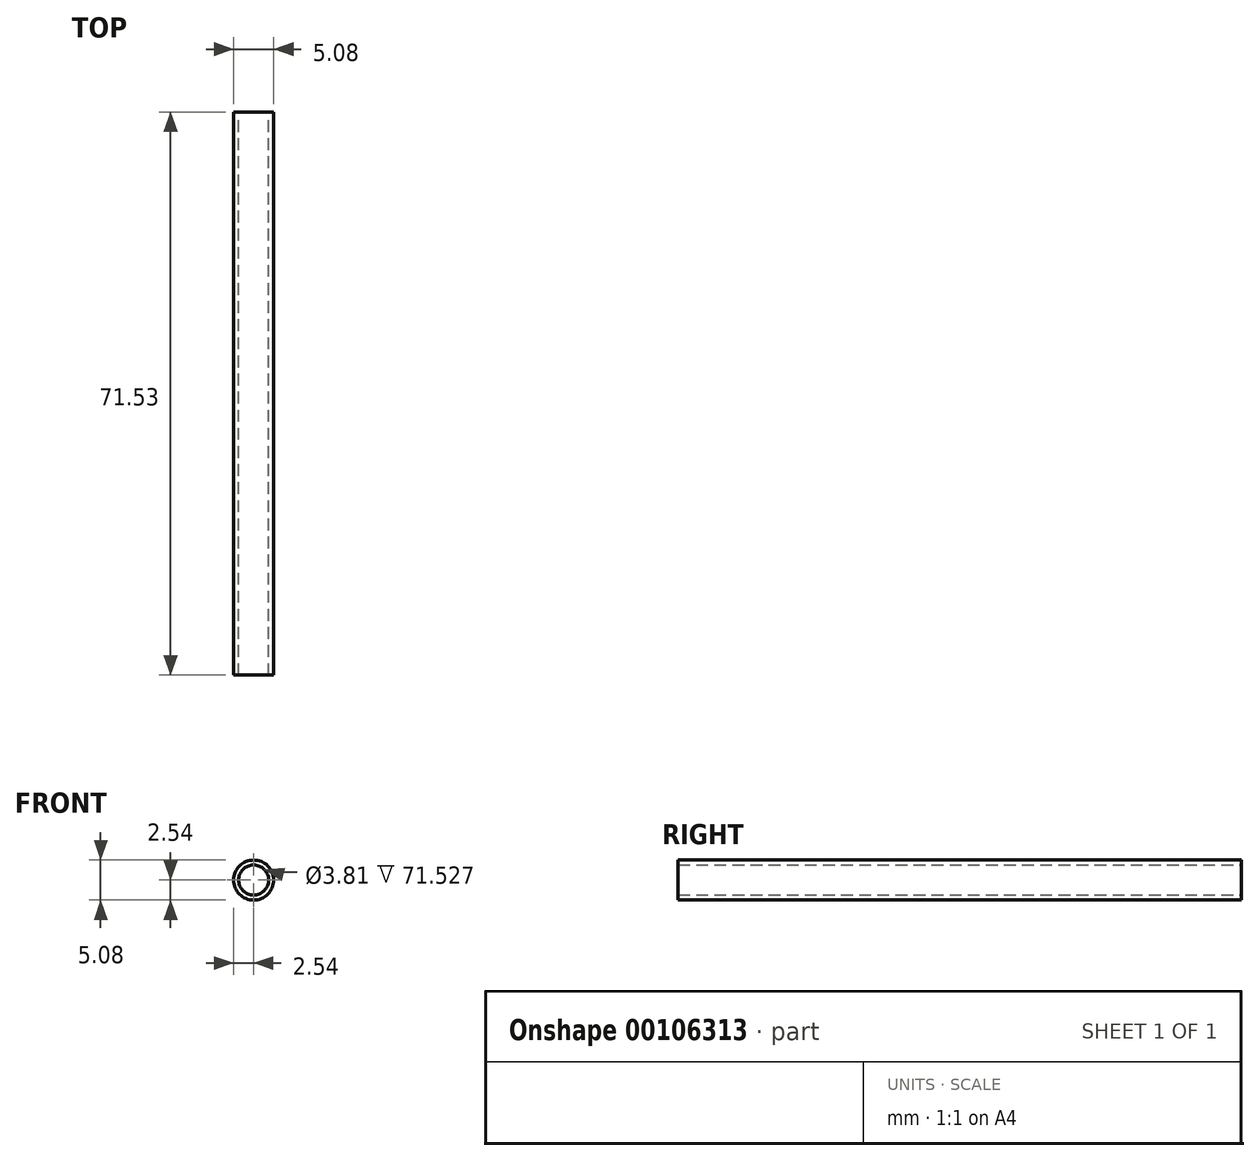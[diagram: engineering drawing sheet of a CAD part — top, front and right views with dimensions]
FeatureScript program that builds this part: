
annotation { "Feature Type Name" : "Feature", "Feature Type Description" : "" }
export const myFeature = defineFeature(function(context is Context, id is Id, definition is map)
    precondition{}
    {
        {
            var Q0;
            Q0=qCreatedBy(makeId("Front.planeOp"),FACE);
            var sketch = newSketch(context, id + "F0", { "sketchPlane" : qUnion([Q0])});
            skCircle(sketch, "E0", {"center": v(0, 0) * mm, "radius": 2.54 * mm});
            skCircle(sketch, "E1", {"center": v(0, 0) * mm, "radius": 1.9 * mm});
            skSolve(sketch);
        }
        {
            var Q0;
            Q0=qCreatedBy(makeId("Top.planeOp"),FACE);
            var sketch = newSketch(context, id + "F1", { "sketchPlane" : qUnion([Q0])});
            skLineSegment(sketch, "E2", {"start": v(0, 0) * mm, "end": v(0, 71.53) * mm});
            skSolve(sketch);
        }
        {
            var Q0;
            Q0 = qSketchRegion(id + "F0", true);
            var Q1;
            Q1 = qConstructionFilter(qBodyType(qCreatedBy(id + "F1" ,EDGE), BodyType.WIRE), ConstructionObject.NO);
            sweep(context, id + "F2", {"profiles" : qUnion([Q0]), "path" : qUnion([Q1])});
        }
    });
